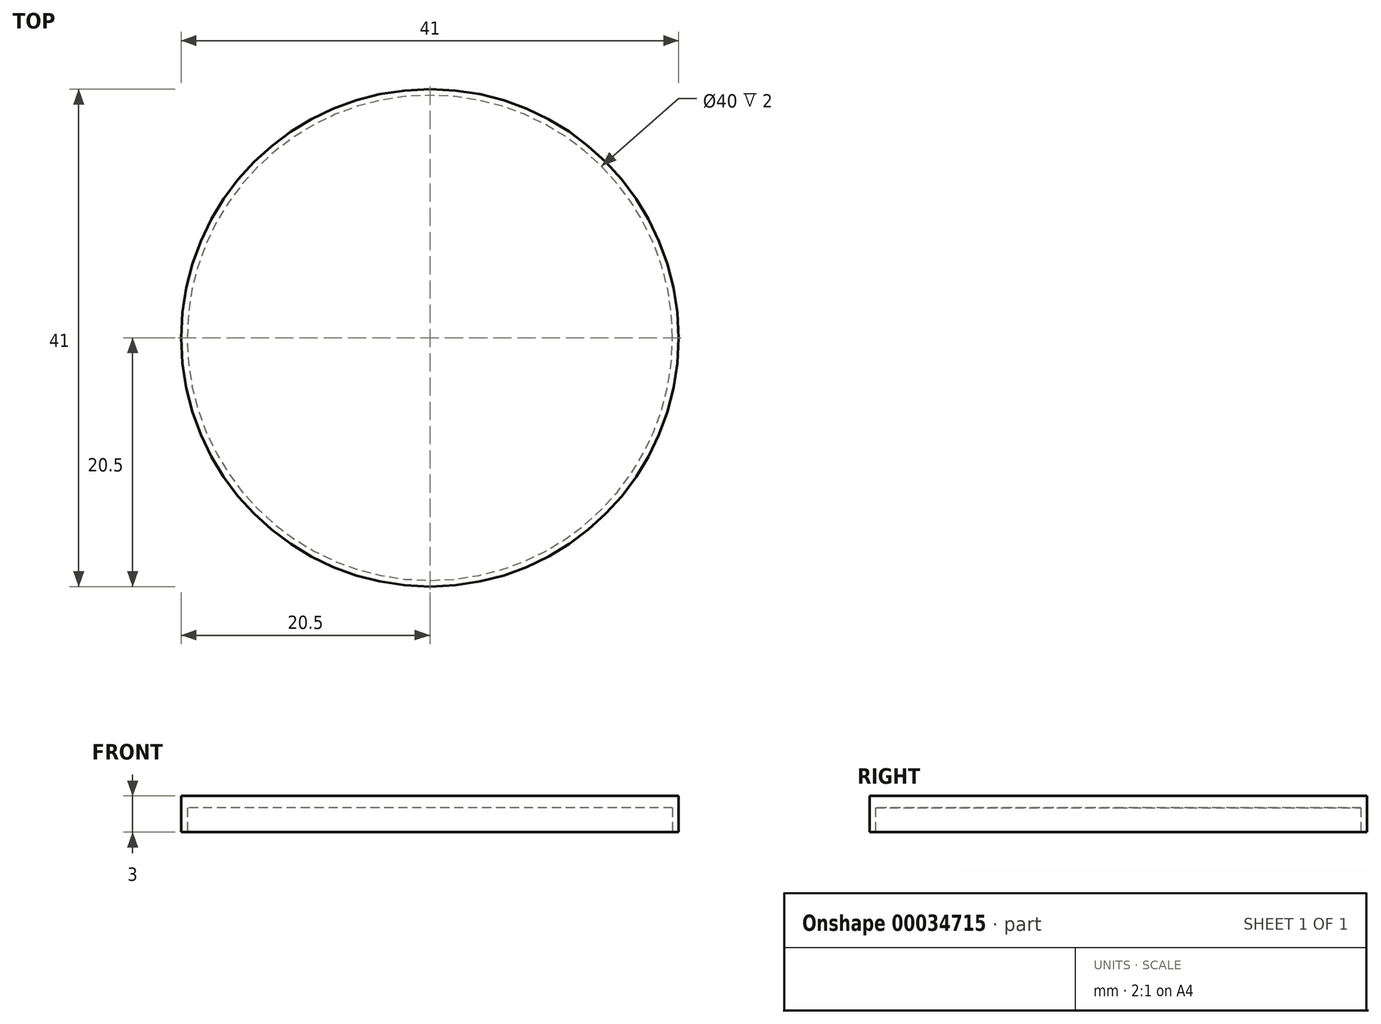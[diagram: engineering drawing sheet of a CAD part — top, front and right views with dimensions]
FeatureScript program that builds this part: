
annotation { "Feature Type Name" : "Feature", "Feature Type Description" : "" }
export const myFeature = defineFeature(function(context is Context, id is Id, definition is map)
    precondition{}
    {
        {
            var Q0;
            Q0=qCreatedBy(makeId("Top.planeOp"),FACE);
            var sketch = newSketch(context, id + "F0", { "sketchPlane" : qUnion([Q0])});
            skCircle(sketch, "E0", {"center": v(0, 0) * mm, "radius": 20 * mm});
            skCircle(sketch, "E1", {"center": v(0, 0) * mm, "radius": 20.5 * mm});
            skSolve(sketch);
        }
        {
            var Q0;
            Q0=makeQuery(id+"F0.imprint","IMPRINT",FACE,{"disambiguationData":[TD([[makeQuery(id+"F0.imprint","IMPRINT",EDGE,{"derivedFrom":sQuery(id+"F0.wireOp",EDGE,"E0")}),-1.0]])]});
            extrude(context, id + "F1", {"entities" : qUnion([Q0]), "depth" : 2 * mm});
        }
        {
            var Q0;
            Q0=makeQuery(id+"F0.imprint","IMPRINT",FACE,{"disambiguationData":[TD([[makeQuery(id+"F0.imprint","IMPRINT",EDGE,{"derivedFrom":sQuery(id+"F0.wireOp",EDGE,"E0")}),1.0]])]});
            var Q1;
            Q1=makeQuery(id+"F0.imprint","IMPRINT",FACE,{"disambiguationData":[TD([[makeQuery(id+"F0.imprint","IMPRINT",EDGE,{"derivedFrom":sQuery(id+"F0.wireOp",EDGE,"E0")}),-1.0]])]});
            extrude(context, id + "F2", {"entities" : qUnion([Q0, Q1]), "operationType" : NewBodyOperationType.ADD, "depth" : 3 * mm, "hasSecondDirection" : true, "secondDirectionOppositeDirection" : false, "secondDirectionDepth" : 2 * mm});
        }
    });
